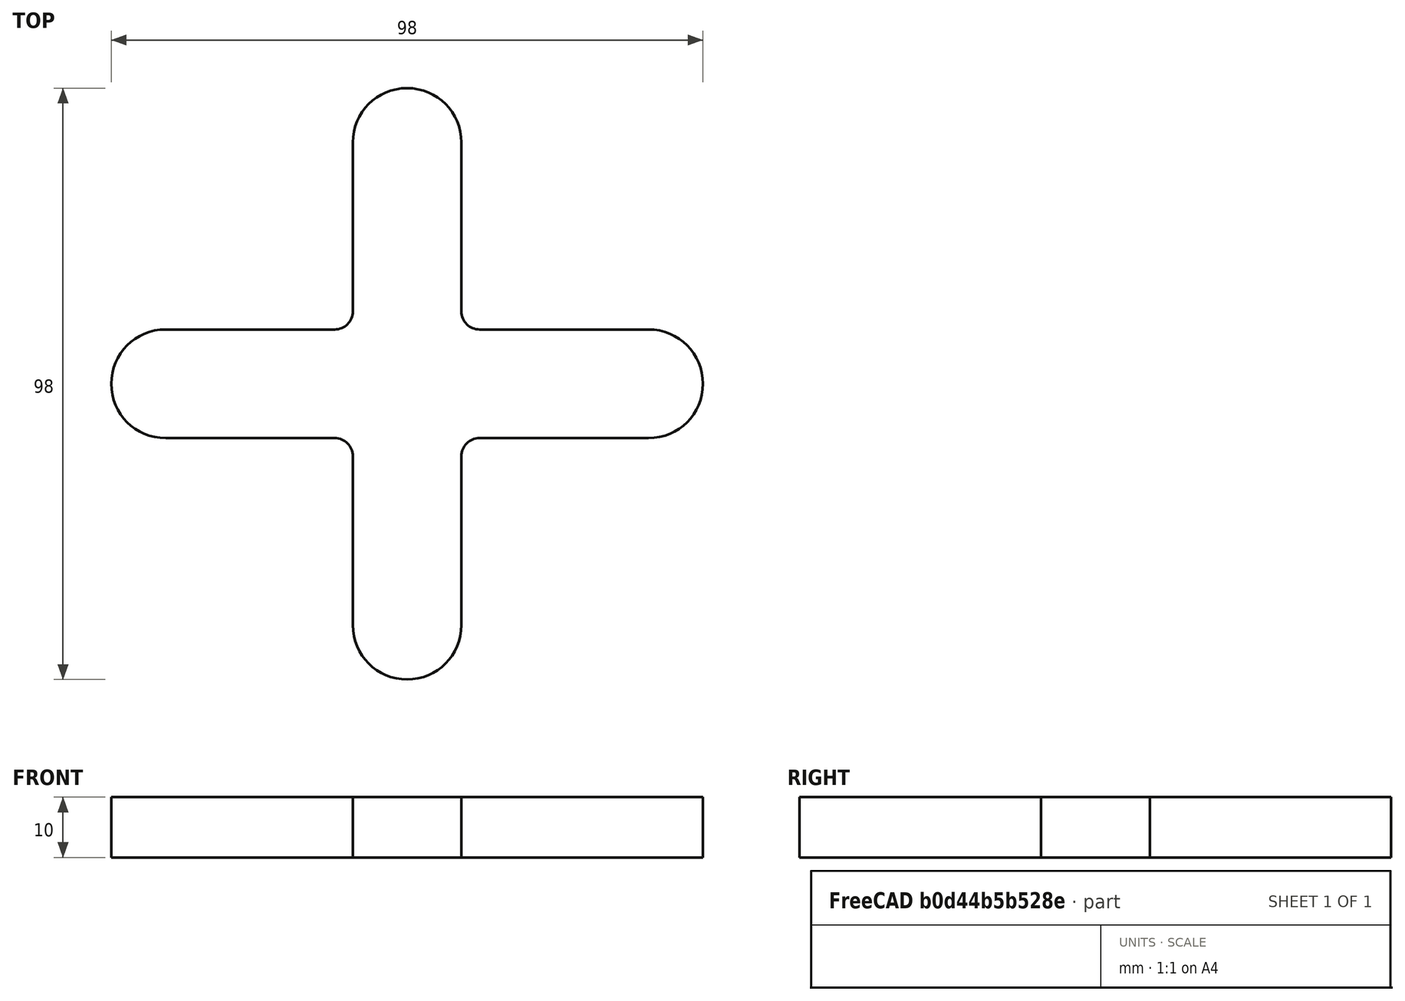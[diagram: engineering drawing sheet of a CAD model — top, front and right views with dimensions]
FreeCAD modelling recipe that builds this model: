
FCSTD DOCUMENT  (FreeCAD 0.16R6707 (Git))
Label: Cruceta
License: CreativeCommons Attribution-ShareAlike
LicenseURL: http://creativecommons.org/licenses/by-sa/4.0/
objects: Sketcher::SketchObject×1, PartDesign::Pad×1
note: 3 computed .brp shape members not serialized (recipe doc carries the construction recipe); baked Part::Feature solids carry a one-line shape summary decoded from their .brp

FEATURE [Sketcher::SketchObject] Sketch  label="BCT_Cruceta"
  sketch-geometry (16):
    g0: LineSegment StartX=-9 StartY=12 StartZ=0 EndX=-9 EndY=40 EndZ=0
    g1: LineSegment StartX=9 StartY=40 StartZ=0 EndX=9 EndY=12 EndZ=0
    g2: LineSegment StartX=12 StartY=9 StartZ=0 EndX=40 EndY=9 EndZ=0
    g3: LineSegment StartX=40 StartY=-9 StartZ=0 EndX=12 EndY=-9 EndZ=0
    g4: LineSegment StartX=9 StartY=-12 StartZ=0 EndX=9 EndY=-40 EndZ=0
    g5: LineSegment StartX=-9 StartY=-40 StartZ=0 EndX=-9 EndY=-12 EndZ=0
    g6: LineSegment StartX=-12 StartY=-9 StartZ=0 EndX=-40 EndY=-9 EndZ=0
    g7: LineSegment StartX=-40 StartY=9 StartZ=0 EndX=-12 EndY=9 EndZ=0
    g8: ArcOfCircle CenterX=0 CenterY=40 CenterZ=0 NormalX=0 NormalY=0 NormalZ=1 Radius=9 StartAngle=0 EndAngle=3.14159
    g9: ArcOfCircle CenterX=-40 CenterY=0 CenterZ=0 NormalX=0 NormalY=0 NormalZ=1 Radius=9 StartAngle=1.5708 EndAngle=4.71239
    g10: ArcOfCircle CenterX=0 CenterY=-40 CenterZ=0 NormalX=0 NormalY=0 NormalZ=1 Radius=9 StartAngle=3.14159 EndAngle=6.28319
    g11: ArcOfCircle CenterX=40 CenterY=0 CenterZ=0 NormalX=0 NormalY=0 NormalZ=1 Radius=9 StartAngle=4.71239 EndAngle=7.85398
    g12: ArcOfCircle CenterX=-12 CenterY=12 CenterZ=0 NormalX=0 NormalY=0 NormalZ=1 Radius=3 StartAngle=4.71239 EndAngle=6.28319
    g13: ArcOfCircle CenterX=12 CenterY=12 CenterZ=0 NormalX=0 NormalY=0 NormalZ=1 Radius=3 StartAngle=3.14159 EndAngle=4.71239
    g14: ArcOfCircle CenterX=12 CenterY=-12 CenterZ=0 NormalX=0 NormalY=0 NormalZ=1 Radius=3 StartAngle=1.5708 EndAngle=3.14159
    g15: ArcOfCircle CenterX=-12 CenterY=-12 CenterZ=0 NormalX=0 NormalY=0 NormalZ=1 Radius=3 StartAngle=0 EndAngle=1.5708
  constraints (40):
    c: Tangent(g0,g8) = 1.5708
    c: Tangent(g1,g8) = 1.5708
    c: Tangent(g7,g9) = 1.5708
    c: Tangent(g6,g9) = 1.5708
    c: Tangent(g5,g10) = 1.5708
    c: Tangent(g4,g10) = 1.5708
    c: Tangent(g3,g11) = 1.5708
    c: Tangent(g2,g11) = 1.5708
    c: PointOnObject(g11,g-1)
    c: PointOnObject(g9,g-1)
    c: PointOnObject(g10,g-2)
    c: PointOnObject(g8,g-2)
    c: Equal(g9,g8)
    c: Equal(g8,g11)
    c: Equal(g11,g10)
    c: Symmetric(g11,g9,g-2)
    c: Symmetric(g8,g10,g-1)
    c: Horizontal(g7)
    c: Horizontal(g2)
    c: Horizontal(g3)
    c: Horizontal(g6)
    c: Vertical(g1)
    c: Vertical(g0)
    c: Vertical(g5)
    c: Vertical(g4)
    c: Equal(g7,g0)
    c: Tangent(g7,g12) = -1.5708
    c: Tangent(g0,g12) = -1.5708
    c: Tangent(g1,g13) = -1.5708
    c: Tangent(g2,g13) = -1.5708
    c: Tangent(g3,g14) = -1.5708
    c: Tangent(g4,g14) = -1.5708
    c: Tangent(g6,g15) = -1.5708
    c: Tangent(g5,g15) = -1.5708
    c: Equal(g15,g12)
    c: Equal(g12,g13)
    c: Equal(g13,g14)
    c: Radius(g11) = 9
    c: Radius(g13) = 3
    c: DistanceX(g9,g11) = 80
FEATURE [PartDesign::Pad] Pad  label="Cruceta"
  Length = 10
  Length2 = 100
  Sketch = -> Sketch
  Type = 0
